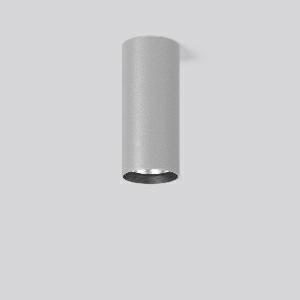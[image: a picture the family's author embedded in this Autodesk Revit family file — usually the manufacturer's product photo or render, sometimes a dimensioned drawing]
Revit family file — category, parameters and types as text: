
# Revit family: heledon_mini_a_931201_004_1_4423
name_source: partatom
category: Lighting Fixtures
units: mm (PartAtom-declared; Revit-internal decimal feet)

## family parameters
Cut with Voids When Loaded = No
Host = Face
Light Source = No
Part Type = Normal
Room Calculation Point = No
Round Connector Dimension = Use Diameter
Shared = No

## types (1)
- HELEDON mini A (1 x LED Modul 940, 2600 lm, 4000)
    Apparent Load = 20 VA
    Approval mark = CE
    CIE Flux Codes = 99 100 100 100 100
    Color Rendering = 92
    Color Temperature = 4000
    Default Elevation = 1800 mm
    Description = Series: HELEDON mini
Cylindrical surface-mounted downlight. Housing: die-cast aluminium, powder-coated. Internal ceiling frame polycarbonate with bayonet mounting. Black plastic ring and recessed LED to prevent glare from the side. Optical assembly with reflector made of MIRO-Silver with 98% total light reflection for outstanding efficiency - can be changed without tools. Best colour rendering index Ra>90. Suitable for Ceiling mounting. Easy installation with a separate ceiling frame with bayonet mounting and plug connection. Driver integrated. Connected via plug-in connector. High quality converter without flickering and stroboscopic effect. The following accessories can be mounted without use of tools: interchangeable lenses, decorative glasses, honeycomb louvre, clear and frosted diffusers, white interchangeable plastic ring. 
Colour: silver
Diameter: 87 mm
Height: 197 mm
Lamp: LED
Socket: without socket
Colour temperature: 4000K
Colour rendering index (CRI): 92
System power: 20 W
Rated luminous flux: 2600 lm
Luminous efficiency: 130 lm/W
Control gear: Regulated power supply
Protection class: I
Type of protection: IP 20
    Height = 197 mm
    Lamp = 1 x LED Modul 940
    Lamp Light Flux = 2600 lm
    Lamp count = 1
    Length = 87 mm
    Lifetime = 50000 h
    Luminous efficacy = 130 lm/W
    Manufacturer = RZB
    ModVariant = No
    Model = 931201.004.1
    Mounting Place = Ceiling
    Mounting Type = Surface mounted
    Number of Poles = 1
    OnlyDefault = Yes
    Power Factor = 1
    Product Name = HELEDON mini A
    Product group = Surface mounted downlights
    ProductGroupID = 302
    Protection Class = Protection class I
    Protection Degree = IP 20
    RLX_Detail_Level = 1
    RLX_Emergency_Light_Flux = 0 lm
    RLX_Emergency_Type = 0
    RLX_Emergency_Type_DB = No
    RlxData = <blob elided: 109317 chars, md5=036d3f25>
    Socket = socket
    Standby Power = 0 W
    System Light Flux = 2600 lm
    System Power = 20 W
    Type Comments = Product without accessories
    Type Image = 931188.004.jpg
    URL = http://relux.com
    VarID = ---
    Voltage = 230 V
    Voltage Range = 220-240 V
    Weight = 0.00 kg
    Width = 0 mm  [stored 0 ft]

note: [stored X ft] marks values corroborated as IEEE doubles in the binary element streams (Revit-internal decimal feet)

## geometry (parser evidence)
native form markers: Blend x4, Sweep x10
no freeform markers — native parametric forms only
